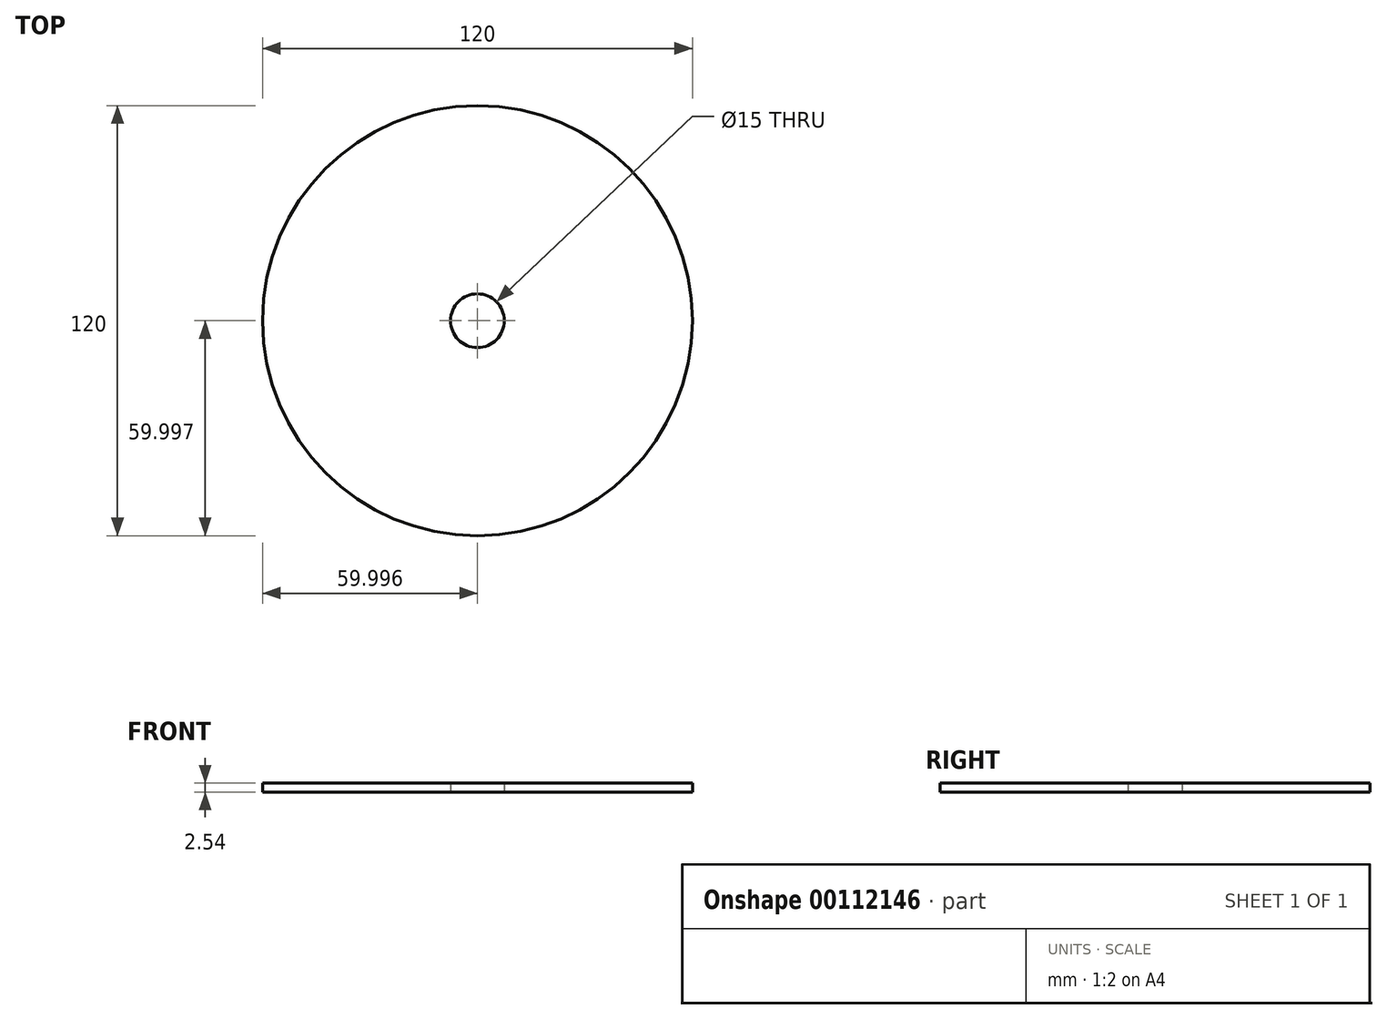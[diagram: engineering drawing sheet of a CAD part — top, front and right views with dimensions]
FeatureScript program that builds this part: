
annotation { "Feature Type Name" : "Feature", "Feature Type Description" : "" }
export const myFeature = defineFeature(function(context is Context, id is Id, definition is map)
    precondition{}
    {
        {
            var Q0;
            Q0=qCreatedBy(makeId("Top.planeOp"),FACE);
            var sketch = newSketch(context, id + "F0", { "sketchPlane" : qUnion([Q0])});
            skCircle(sketch, "E0", {"center": v(-38.32, -43.9) * mm, "radius": 60 * mm});
            skCircle(sketch, "E1", {"center": v(-38.32, -43.9) * mm, "radius": 7.5 * mm});
            skSolve(sketch);
        }
        {
            var Q0;
            Q0=makeQuery(id+"F0.imprint","IMPRINT",FACE,{"disambiguationData":[TD([[makeQuery(id+"F0.imprint","IMPRINT",EDGE,{"derivedFrom":sQuery(id+"F0.wireOp",EDGE,"E0")}),1.0]])]});
            extrude(context, id + "F1", {"entities" : qUnion([Q0]), "depth" : 2.54 * mm});
        }
    });
